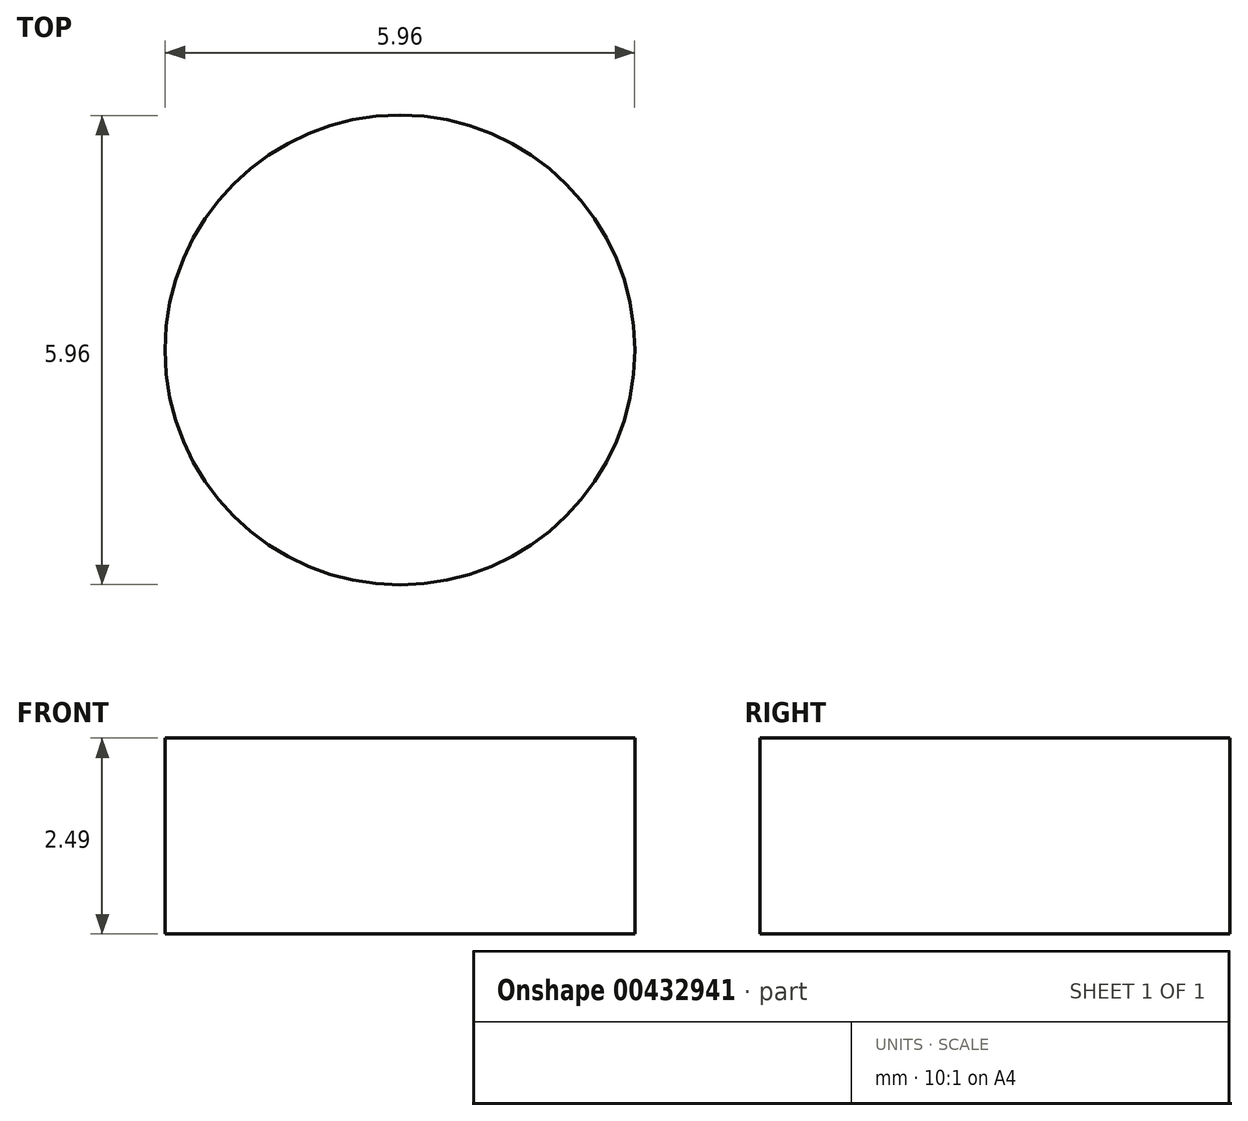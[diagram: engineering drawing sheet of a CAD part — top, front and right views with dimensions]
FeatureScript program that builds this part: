
annotation { "Feature Type Name" : "Feature", "Feature Type Description" : "" }
export const myFeature = defineFeature(function(context is Context, id is Id, definition is map)
    precondition{}
    {
        {
            var Q0;
            Q0=qCreatedBy(makeId("Top.planeOp"),FACE);
            var sketch = newSketch(context, id + "F0", { "sketchPlane" : qUnion([Q0])});
            skCircle(sketch, "E0", {"center": v(0, 0) * mm, "radius": 2.98 * mm});
            skSolve(sketch);
        }
        {
            var Q0;
            Q0=qSketchRegion(id+"F0",true);
            extrude(context, id + "F1", {"entities" : qUnion([Q0]), "depth" : 2.5 * mm});
        }
    });
